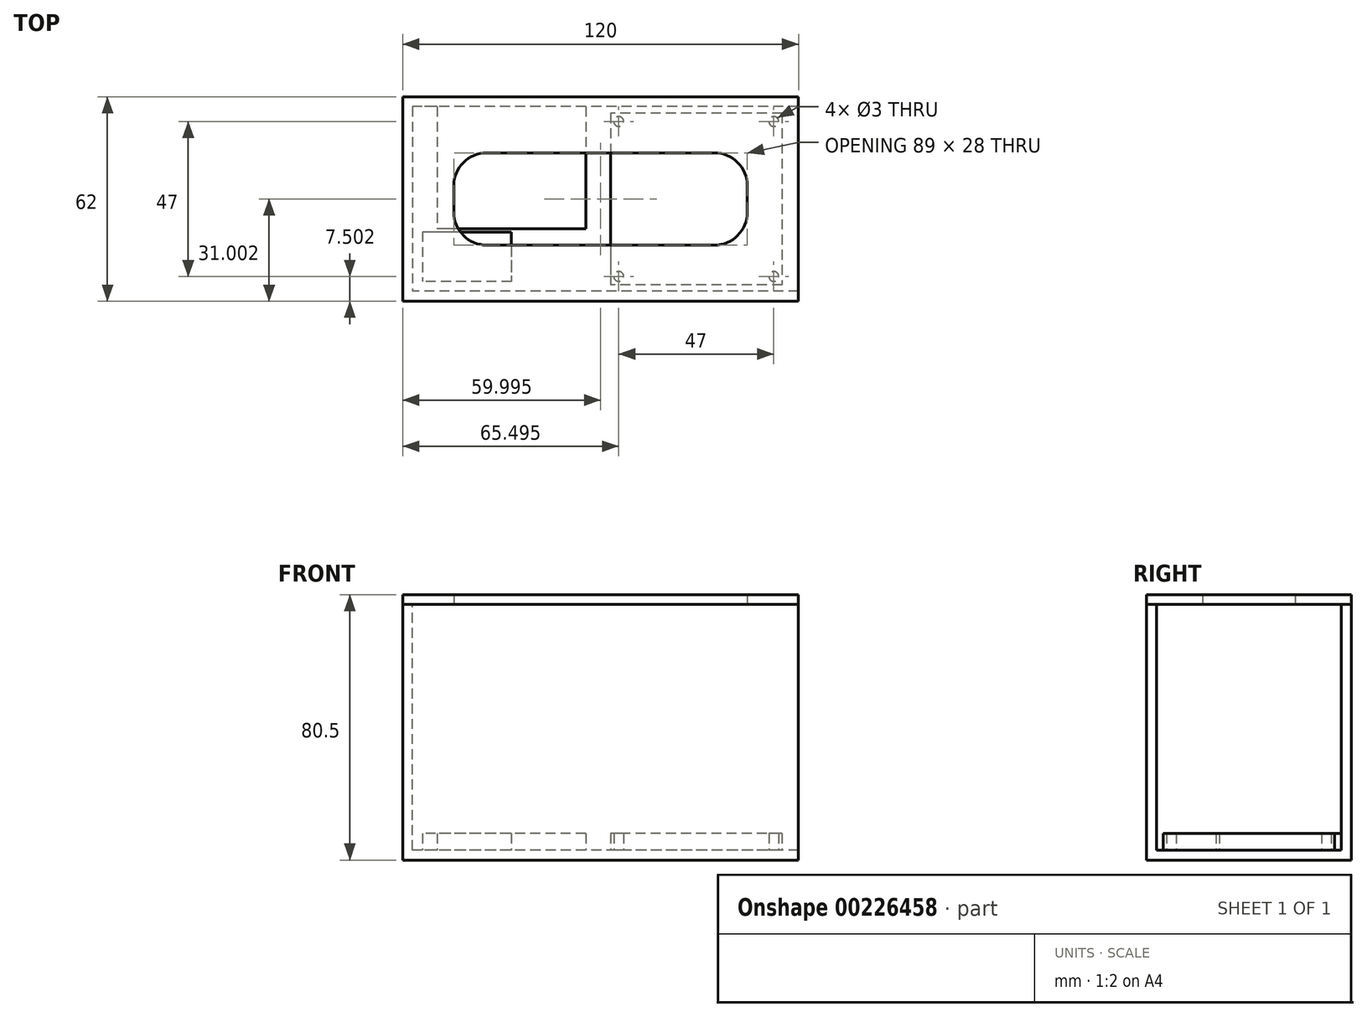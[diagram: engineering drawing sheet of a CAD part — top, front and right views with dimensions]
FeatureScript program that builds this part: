
annotation { "Feature Type Name" : "Feature", "Feature Type Description" : "" }
export const myFeature = defineFeature(function(context is Context, id is Id, definition is map)
    precondition{}
    {
        {
            var Q0;
            Q0=qCreatedBy(makeId("Top.planeOp"),FACE);
            var sketch = newSketch(context, id + "F0", { "sketchPlane" : qUnion([Q0])});
            skLineSegment(sketch, "E0.bottom", {"start": v(55.38, 14.81) * mm, "end": v(-64.62, 14.81) * mm});
            skLineSegment(sketch, "E0.top", {"start": v(55.38, -47.19) * mm, "end": v(-64.62, -47.19) * mm});
            skLineSegment(sketch, "E0.left", {"start": v(55.38, 14.81) * mm, "end": v(55.38, -47.19) * mm});
            skLineSegment(sketch, "E0.right", {"start": v(-64.62, 14.81) * mm, "end": v(-64.62, -47.19) * mm});
            skPoint(sketch, "E0.middle", {"position": v(-4.62, -16.19) * mm});
            skSolve(sketch);
        }
        {
            var Q0;
            Q0=makeQuery(id+"F0.imprint","IMPRINT",FACE,{"disambiguationData":[TD([[makeQuery(id+"F0.imprint","IMPRINT",EDGE,{"derivedFrom":sQuery(id+"F0.wireOp",EDGE,"E0.bottom")}),1.0]])]});
            extrude(context, id + "F1", {"entities" : qUnion([Q0]), "depth" : 77.5 * mm});
        }
        {
            var Q0;
            Q0=makeQuery(id+"F1.opExtrude","CAP_FACE",FACE,{"disambiguationData":[OSD([sQuery(id+"F0.wireOp",EDGE,"E0.bottom"),sQuery(id+"F0.wireOp",EDGE,"E0.top"),sQuery(id+"F0.wireOp",EDGE,"E0.left"),sQuery(id+"F0.wireOp",EDGE,"E0.right")])],"isStart":false});
            var sketch = newSketch(context, id + "F2", { "sketchPlane" : qUnion([Q0])});
            skLineSegment(sketch, "E1.bottom", {"start": v(55.38, 11.81) * mm, "end": v(-61.62, 11.81) * mm});
            skLineSegment(sketch, "E1.top", {"start": v(55.38, -44.19) * mm, "end": v(-61.62, -44.19) * mm});
            skLineSegment(sketch, "E1.left", {"start": v(55.38, 11.81) * mm, "end": v(55.38, -44.19) * mm});
            skLineSegment(sketch, "E1.right", {"start": v(-61.62, 11.81) * mm, "end": v(-61.62, -44.19) * mm});
            skPoint(sketch, "E1.middle", {"position": v(-3.12, -16.19) * mm});
            skLineSegment(sketch, "E2", {"start": v(24.78, 11.81) * mm, "end": v(24.78, 14.81) * mm});
            skLineSegment(sketch, "E3", {"start": v(24.55, -44.19) * mm, "end": v(24.55, -47.19) * mm});
            skLineSegment(sketch, "E4", {"start": v(-61.62, -16.19) * mm, "end": v(-64.62, -16.19) * mm});
            skSolve(sketch);
        }
        {
            var Q0;
            {var subQ4=sQuery(id+"F2.wireOp",EDGE,"E1.left");var subQ6=sQuery(id+"F2.wireOp",EDGE,"E1.bottom");var subQ9=makeQuery(id+"F2.imprint","INTERSECT",VERTEX,{"derivedFrom":[subQ6,subQ4]});Q0=makeQuery(id+"F2.imprint","IMPRINT",FACE,{"disambiguationData":[TD([[makeQuery(id+"F2.imprint","IMPRINT",EDGE,{"disambiguationData":[TD([[subQ9,-1.0]])],"derivedFrom":subQ6}),1.0]])]});}
            extrude(context, id + "F3", {"entities" : qUnion([Q0]), "operationType" : NewBodyOperationType.REMOVE, "oppositeDirection" : true, "depth" : 74.5 * mm});
        }
        {
            var Q0;
            Q0=makeQuery(id+"F1.opExtrude","CAP_FACE",FACE,{"disambiguationData":[OSD([sQuery(id+"F0.wireOp",EDGE,"E0.bottom"),sQuery(id+"F0.wireOp",EDGE,"E0.top"),sQuery(id+"F0.wireOp",EDGE,"E0.left"),sQuery(id+"F0.wireOp",EDGE,"E0.right")])],"isStart":false});
            var sketch = newSketch(context, id + "F4", { "sketchPlane" : qUnion([Q0])});
            skLineSegment(sketch, "E5.bottom", {"start": v(-64.62, 14.81) * mm, "end": v(55.38, 14.81) * mm});
            skLineSegment(sketch, "E5.top", {"start": v(-64.62, -47.19) * mm, "end": v(55.38, -47.19) * mm});
            skLineSegment(sketch, "E5.left", {"start": v(-64.62, 14.81) * mm, "end": v(-64.62, -47.19) * mm});
            skLineSegment(sketch, "E5.right", {"start": v(55.38, 14.81) * mm, "end": v(55.38, -47.19) * mm});
            skLineSegment(sketch, "E6.bottom", {"start": v(-39.12, -2.19) * mm, "end": v(29.88, -2.19) * mm});
            skLineSegment(sketch, "E6.top", {"start": v(-39.12, -30.19) * mm, "end": v(29.88, -30.19) * mm});
            skLineSegment(sketch, "E6.left", {"start": v(-49.12, -12.19) * mm, "end": v(-49.12, -20.19) * mm});
            skLineSegment(sketch, "E6.right", {"start": v(39.88, -12.19) * mm, "end": v(39.88, -20.19) * mm});
            skPoint(sketch, "E7.visualSharp", {"position": v(-49.12, -2.19) * mm});
            skArc(sketch, "E7.filletArc", {"start": v(-39.12, -2.19) * mm, "mid": v(-46.2, -5.12) * mm, "end": v(-49.12, -12.19) * mm});
            skPoint(sketch, "E8.visualSharp", {"position": v(-49.12, -30.19) * mm});
            skArc(sketch, "E8.filletArc", {"start": v(-49.12, -20.19) * mm, "mid": v(-46.2, -27.26) * mm, "end": v(-39.12, -30.19) * mm});
            skPoint(sketch, "E9.visualSharp", {"position": v(39.88, -2.19) * mm});
            skArc(sketch, "E9.filletArc", {"start": v(39.88, -12.19) * mm, "mid": v(36.95, -5.12) * mm, "end": v(29.88, -2.19) * mm});
            skPoint(sketch, "E10.visualSharp", {"position": v(39.88, -30.19) * mm});
            skArc(sketch, "E10.filletArc", {"start": v(29.88, -30.19) * mm, "mid": v(36.95, -27.26) * mm, "end": v(39.88, -20.19) * mm});
            skLineSegment(sketch, "E11", {"start": v(-21.7, -2.19) * mm, "end": v(-21.7, 14.81) * mm});
            skLineSegment(sketch, "E12", {"start": v(55.38, -18.83) * mm, "end": v(39.88, -18.83) * mm});
            skLineSegment(sketch, "E13", {"start": v(-20.47, -30.19) * mm, "end": v(-20.47, -47.19) * mm});
            skLineSegment(sketch, "E14", {"start": v(-49.12, -18.26) * mm, "end": v(-64.62, -18.26) * mm});
            skSolve(sketch);
        }
        {
            var Q0;
            {var subQ1=sQuery(id+"F4.wireOp",EDGE,"E5.left");var subQ6=sQuery(id+"F4.wireOp",EDGE,"E5.bottom");var subQ10=makeQuery(id+"F4.imprint","INTERSECT",VERTEX,{"derivedFrom":[subQ6,subQ1]});Q0=makeQuery(id+"F4.imprint","IMPRINT",FACE,{"disambiguationData":[TD([[makeQuery(id+"F4.imprint","IMPRINT",EDGE,{"disambiguationData":[TD([[subQ10,1.0]])],"derivedFrom":subQ6}),1.0]])]});}
            var Q1;
            {var subQ9=sQuery(id+"F4.wireOp",EDGE,"E7.filletArc");Q1=makeQuery(id+"F4.imprint","IMPRINT",FACE,{"disambiguationData":[TD([[makeQuery(id+"F4.imprint","IMPRINT",EDGE,{"derivedFrom":subQ9}),-1.0]])]});}
            var Q2;
            {var subQ0=sQuery(id+"F4.wireOp",EDGE,"E9.filletArc");Q2=makeQuery(id+"F4.imprint","IMPRINT",FACE,{"disambiguationData":[TD([[makeQuery(id+"F4.imprint","IMPRINT",EDGE,{"derivedFrom":subQ0}),-1.0]])]});}
            var Q3;
            {var subQ0=sQuery(id+"F4.wireOp",EDGE,"E10.filletArc");Q3=makeQuery(id+"F4.imprint","IMPRINT",FACE,{"disambiguationData":[TD([[makeQuery(id+"F4.imprint","IMPRINT",EDGE,{"derivedFrom":subQ0}),-1.0]])]});}
            var Q4;
            {var subQ1=sQuery(id+"F4.wireOp",EDGE,"E5.top");var subQ5=sQuery(id+"F4.wireOp",EDGE,"E5.left");var subQ6=makeQuery(id+"F4.imprint","INTERSECT",VERTEX,{"derivedFrom":[subQ1,subQ5]});Q4=makeQuery(id+"F4.imprint","IMPRINT",FACE,{"disambiguationData":[TD([[makeQuery(id+"F4.imprint","IMPRINT",EDGE,{"disambiguationData":[TD([[subQ6,1.0]])],"derivedFrom":subQ1}),-1.0]])]});}
            var Q5;
            {var subQ0=sQuery(id+"F4.wireOp",EDGE,"E8.filletArc");Q5=makeQuery(id+"F4.imprint","IMPRINT",FACE,{"disambiguationData":[TD([[makeQuery(id+"F4.imprint","IMPRINT",EDGE,{"derivedFrom":subQ0}),-1.0]])]});}
            var Q6;
            {var subQ0=sQuery(id+"F4.wireOp",EDGE,"E5.right");var subQ1=sQuery(id+"F4.wireOp",EDGE,"E5.top");var subQ2=makeQuery(id+"F4.imprint","INTERSECT",VERTEX,{"derivedFrom":[subQ1,subQ0]});Q6=makeQuery(id+"F4.imprint","IMPRINT",FACE,{"disambiguationData":[TD([[makeQuery(id+"F4.imprint","IMPRINT",EDGE,{"disambiguationData":[TD([[subQ2,-1.0]])],"derivedFrom":subQ1}),-1.0]])]});}
            var Q7;
            {var subQ0=sQuery(id+"F4.wireOp",EDGE,"E5.right");var subQ1=sQuery(id+"F4.wireOp",EDGE,"E5.bottom");var subQ2=makeQuery(id+"F4.imprint","INTERSECT",VERTEX,{"derivedFrom":[subQ1,subQ0]});Q7=makeQuery(id+"F4.imprint","IMPRINT",FACE,{"disambiguationData":[TD([[makeQuery(id+"F4.imprint","IMPRINT",EDGE,{"disambiguationData":[TD([[subQ2,-1.0]])],"derivedFrom":subQ1}),1.0]])]});}
            extrude(context, id + "F5", {"entities" : qUnion([Q0, Q1, Q2, Q3, Q4, Q5, Q6, Q7]), "depth" : 3 * mm});
        }
        {
            var Q0;
            Q0=makeQuery(id+"F3.boolean.opBoolean","COPY",FACE,{"derivedFrom":makeQuery(id+"F3.opExtrude","CAP_FACE",FACE,{"disambiguationData":[OSD([sQuery(id+"F2.wireOp",EDGE,"E1.bottom"),sQuery(id+"F2.wireOp",EDGE,"E1.top"),sQuery(id+"F2.wireOp",EDGE,"E1.left"),sQuery(id+"F2.wireOp",EDGE,"E1.right")])],"isStart":false})});
            var sketch = newSketch(context, id + "F6", { "sketchPlane" : qUnion([Q0])});
            skLineSegment(sketch, "E15.bottom", {"start": v(50.38, 9.81) * mm, "end": v(-1.62, 9.81) * mm});
            skLineSegment(sketch, "E15.top", {"start": v(50.38, -42.19) * mm, "end": v(-1.62, -42.19) * mm});
            skLineSegment(sketch, "E15.left", {"start": v(50.38, 9.81) * mm, "end": v(50.38, -42.19) * mm});
            skLineSegment(sketch, "E15.right", {"start": v(-1.62, 9.81) * mm, "end": v(-1.62, -42.19) * mm});
            skLineSegment(sketch, "E16", {"start": v(24.38, 9.81) * mm, "end": v(24.38, 11.81) * mm});
            skLineSegment(sketch, "E17", {"start": v(24.38, -42.19) * mm, "end": v(24.38, -44.19) * mm});
            skLineSegment(sketch, "E18", {"start": v(-1.62, -13.12) * mm, "end": v(-61.62, -13.12) * mm});
            skLineSegment(sketch, "E19", {"start": v(50.38, -13.58) * mm, "end": v(55.38, -13.58) * mm});
            skLineSegment(sketch, "E20.bottom", {"start": v(3.38, -37.19) * mm, "end": v(45.38, -37.19) * mm});
            skLineSegment(sketch, "E20.top", {"start": v(3.38, 4.81) * mm, "end": v(45.38, 4.81) * mm});
            skLineSegment(sketch, "E20.left", {"start": v(3.38, -37.19) * mm, "end": v(3.38, 4.81) * mm});
            skLineSegment(sketch, "E20.right", {"start": v(45.38, -37.19) * mm, "end": v(45.38, 4.81) * mm});
            skLineSegment(sketch, "E21", {"start": v(3.38, -37.19) * mm, "end": v(-1.62, -42.19) * mm});
            skLineSegment(sketch, "E22", {"start": v(3.38, 4.81) * mm, "end": v(-1.62, 9.81) * mm});
            skLineSegment(sketch, "E23", {"start": v(50.38, 9.81) * mm, "end": v(45.38, 4.81) * mm});
            skLineSegment(sketch, "E24", {"start": v(45.38, -37.19) * mm, "end": v(50.38, -42.19) * mm});
            skCircle(sketch, "E25", {"center": v(0.88, 7.31) * mm, "radius": 1.5 * mm});
            skLineSegment(sketch, "E26", {"start": v(-1.62, -13.12) * mm, "end": v(3.38, -13.12) * mm});
            skCircle(sketch, "E27", {"center": v(47.88, 7.31) * mm, "radius": 1.5 * mm});
            skCircle(sketch, "E28", {"center": v(47.88, -39.69) * mm, "radius": 1.5 * mm});
            skCircle(sketch, "E29", {"center": v(0.88, -39.69) * mm, "radius": 1.5 * mm});
            skSolve(sketch);
        }
        {
            var Q0;
            {var subQ5=sQuery(id+"F6.wireOp",EDGE,"E20.right");Q0=makeQuery(id+"F6.imprint","IMPRINT",FACE,{"disambiguationData":[TD([[makeQuery(id+"F6.imprint","IMPRINT",EDGE,{"derivedFrom":subQ5}),-1.0]])]});}
            var Q1;
            {var subQ0=sQuery(id+"F6.wireOp",EDGE,"E20.top");Q1=makeQuery(id+"F6.imprint","IMPRINT",FACE,{"disambiguationData":[TD([[makeQuery(id+"F6.imprint","IMPRINT",EDGE,{"derivedFrom":subQ0}),1.0]])]});}
            var Q2;
            {var subQ8=sQuery(id+"F6.wireOp",EDGE,"E26");Q2=makeQuery(id+"F6.imprint","IMPRINT",FACE,{"disambiguationData":[TD([[makeQuery(id+"F6.imprint","IMPRINT",EDGE,{"derivedFrom":subQ8}),1.0]])]});}
            var Q3;
            {var subQ7=sQuery(id+"F6.wireOp",EDGE,"E26");Q3=makeQuery(id+"F6.imprint","IMPRINT",FACE,{"disambiguationData":[TD([[makeQuery(id+"F6.imprint","IMPRINT",EDGE,{"derivedFrom":subQ7}),-1.0]])]});}
            var Q4;
            {var subQ3=sQuery(id+"F6.wireOp",EDGE,"E20.bottom");Q4=makeQuery(id+"F6.imprint","IMPRINT",FACE,{"disambiguationData":[TD([[makeQuery(id+"F6.imprint","IMPRINT",EDGE,{"derivedFrom":subQ3}),1.0]])]});}
            var Q5;
            {var subQ4=sQuery(id+"F6.wireOp",EDGE,"E20.bottom");Q5=makeQuery(id+"F6.imprint","IMPRINT",FACE,{"disambiguationData":[TD([[makeQuery(id+"F6.imprint","IMPRINT",EDGE,{"derivedFrom":subQ4}),-1.0]])]});}
            extrude(context, id + "F7", {"entities" : qUnion([Q0, Q1, Q2, Q3, Q4, Q5]), "depth" : 5.08 * mm});
        }
        {
            var Q0;
            Q0=makeQuery(id+"F3.boolean.opBoolean","COPY",FACE,{"derivedFrom":makeQuery(id+"F3.opExtrude","CAP_FACE",FACE,{"disambiguationData":[OSD([sQuery(id+"F2.wireOp",EDGE,"E1.bottom"),sQuery(id+"F2.wireOp",EDGE,"E1.top"),sQuery(id+"F2.wireOp",EDGE,"E1.left"),sQuery(id+"F2.wireOp",EDGE,"E1.right")])],"isStart":false})});
            var sketch = newSketch(context, id + "F8", { "sketchPlane" : qUnion([Q0])});
            skLineSegment(sketch, "E30.bottom", {"start": v(-31.62, -26.19) * mm, "end": v(-58.62, -26.19) * mm});
            skLineSegment(sketch, "E30.top", {"start": v(-31.62, -41.19) * mm, "end": v(-58.62, -41.19) * mm});
            skLineSegment(sketch, "E30.left", {"start": v(-31.62, -26.19) * mm, "end": v(-31.62, -41.19) * mm});
            skLineSegment(sketch, "E30.right", {"start": v(-58.62, -26.19) * mm, "end": v(-58.62, -41.19) * mm});
            skPoint(sketch, "E30.middle", {"position": v(-45.12, -33.69) * mm});
            skLineSegment(sketch, "E31", {"start": v(-45.12, -41.19) * mm, "end": v(-45.12, -44.19) * mm});
            skLineSegment(sketch, "E32", {"start": v(-58.62, -33.69) * mm, "end": v(-61.62, -33.69) * mm});
            skSolve(sketch);
        }
        {
            var Q0;
            {var subQ5=sQuery(id+"F8.wireOp",EDGE,"E30.bottom");Q0=makeQuery(id+"F8.imprint","IMPRINT",FACE,{"disambiguationData":[TD([[makeQuery(id+"F8.imprint","IMPRINT",EDGE,{"derivedFrom":subQ5}),1.0]])]});}
            extrude(context, id + "F9", {"entities" : qUnion([Q0]), "operationType" : NewBodyOperationType.ADD, "depth" : 5.08 * mm});
        }
        {
            var Q0;
            Q0=makeQuery(id+"F3.boolean.opBoolean","COPY",FACE,{"derivedFrom":makeQuery(id+"F3.opExtrude","CAP_FACE",FACE,{"disambiguationData":[OSD([sQuery(id+"F2.wireOp",EDGE,"E1.bottom"),sQuery(id+"F2.wireOp",EDGE,"E1.top"),sQuery(id+"F2.wireOp",EDGE,"E1.left"),sQuery(id+"F2.wireOp",EDGE,"E1.right")])],"isStart":false})});
            var sketch = newSketch(context, id + "F10", { "sketchPlane" : qUnion([Q0])});
            skLineSegment(sketch, "E33.bottom", {"start": v(-9.12, 11.83) * mm, "end": v(-54.12, 11.83) * mm});
            skLineSegment(sketch, "E33.top", {"start": v(-9.12, -25.17) * mm, "end": v(-54.12, -25.17) * mm});
            skLineSegment(sketch, "E33.left", {"start": v(-9.12, 11.83) * mm, "end": v(-9.12, -25.17) * mm});
            skLineSegment(sketch, "E33.right", {"start": v(-54.12, 11.83) * mm, "end": v(-54.12, -25.17) * mm});
            skPoint(sketch, "E33.middle", {"position": v(-31.62, -6.67) * mm});
            skLineSegment(sketch, "E34", {"start": v(-54.12, -6.67) * mm, "end": v(-61.62, -6.67) * mm});
            skSolve(sketch);
        }
        {
            var Q0;
            {var subQ6=sQuery(id+"F10.wireOp",EDGE,"E33.top");Q0=makeQuery(id+"F10.imprint","IMPRINT",FACE,{"disambiguationData":[TD([[makeQuery(id+"F10.imprint","IMPRINT",EDGE,{"derivedFrom":subQ6}),-1.0]])]});}
            extrude(context, id + "F11", {"entities" : qUnion([Q0]), "operationType" : NewBodyOperationType.ADD, "depth" : 5.08 * mm});
        }
    });
